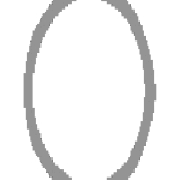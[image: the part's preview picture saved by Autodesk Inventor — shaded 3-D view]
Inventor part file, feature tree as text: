
AUTODESK INVENTOR PART (.ipt)
format: ipt  version: 2021 (Build 250183000, 183)  size: 112,128 bytes
history: native  units: in
note: dims shown in document units (in); Inventor stores cm internally (conversion verified against a paired STEP export)
features: other x4, sketch x3, plane x1
ambient origin geometry x8: Origin, YZ Plane, XZ Plane, XY Plane, X Axis, Y Axis, Z Axis, Center Point
bodies: Solid1 (feature_tree), Body (feature_tree)
feature tree (8):
  other  "Driven Length"
  other  "Frame Generator"
  other  "Start Plane"
  other  "End Plane"
  sketch  "Sketch"  dims[d2=31.4083in d4=-0.0in d5=31.4083in d6=0.12in d7=0.0in d8=90.0deg d9=31.4083in]
  sketch  "Sketch2"  dims[d0=1.0in]
  plane  "Work Plane3"
  sketch  "Sketch3"  dims[d1=0.065in]
